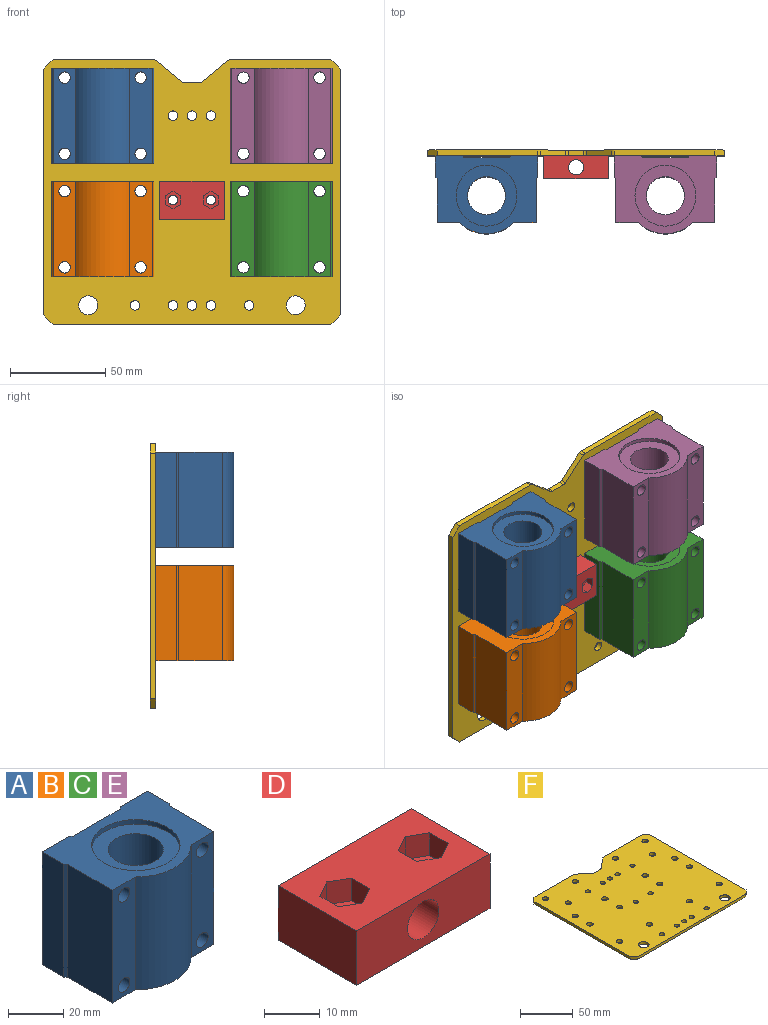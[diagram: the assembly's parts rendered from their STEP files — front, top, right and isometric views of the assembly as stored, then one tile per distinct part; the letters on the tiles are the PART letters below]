
ASSEMBLY  parts=6 mates=5
PART A: 25 faces, bbox 54x41x50 mm
  f0: cylinder r=10mm len=46mm, axis (0,0,1), area 2890.3mm2, adj f23,f24
  f1: cylinder r=16mm len=32mm, axis (0,0,1), area 201.1mm2, adj f22,f23
  f2: cylinder r=16mm len=32mm, axis (0,0,1), area 201.1mm2, adj f7,f24
  f3: cylinder r=3mm len=35mm, axis (0,-1,0), area 659.7mm2, adj f12,f16
  f4: cylinder r=3mm len=35mm, axis (0,-1,0), area 659.7mm2, adj f12,f16
  f5: cylinder r=3mm len=35mm, axis (0,-1,0), area 659.7mm2, adj f10,f20
  f6: cylinder r=3mm len=35mm, axis (0,-1,0), area 659.7mm2, adj f10,f20
  f7: plane 54x41mm, normal (0,0,-1), area 1132mm2, adj f2,f8,f9,f10,f11,f12,f13,f14
  f8: plane 50x1mm, normal (0.71,-0.71,0), area 70.7mm2, adj f7,f9,f21,f22
  f9: plane 50x23mm, normal (1,0,0), area 1150mm2, adj f7,f8,f10,f22
  f10: plane 50x11.72mm, normal (0,-1,0), area 529.3mm2, adj f5,f6,f7,f9,f11,f22
  f11: cylinder r=20mm len=50mm, axis (0,0,1), area 1590.8mm2, adj f7,f10,f12,f22
  f12: plane 50x11.72mm, normal (0,-1,0), area 529.3mm2, adj f3,f4,f7,f11,f13,f22
  f13: plane 50x23mm, normal (-1,0,0), area 1150mm2, adj f7,f12,f14,f22
  f14: plane 50x1mm, normal (-0.71,-0.71,0), area 70.7mm2, adj f7,f13,f15,f22
  f15: plane 50x11mm, normal (-1,0,0), area 550mm2, adj f7,f14,f16,f22
  f16: plane 50x14mm, normal (0,1,0), area 643.5mm2, adj f3,f4,f7,f15,f17,f22
  f17: plane 50x1mm, normal (0.71,0.71,0), area 70.7mm2, adj f7,f16,f18,f22
  f18: plane 50x24mm, normal (0,1,0), area 1200mm2, adj f7,f17,f19,f22
  f19: plane 50x1mm, normal (-0.71,0.71,0), area 70.7mm2, adj f7,f18,f20,f22
  f20: plane 50x14mm, normal (0,1,0), area 643.5mm2, adj f5,f6,f7,f19,f21,f22
  f21: plane 50x11mm, normal (1,0,0), area 550mm2, adj f7,f8,f20,f22
  f22: plane 54x41mm, normal (0,0,1), area 1132mm2, adj f1,f8,f9,f10,f11,f12,f13,f14
  f23: plane 32x32mm, normal (0,0,1), area 490.1mm2, adj f0,f1
  f24: plane 32x32mm, normal (0,0,-1), area 490.1mm2, adj f0,f2
PART B: same geometry as A
PART C: same geometry as A
PART D: 27 faces, bbox 34x20x12 mm
  f0: cylinder r=4.5mm len=9mm, axis (0,0,-1), area 56.5mm2, adj f6,f26
  f1: cylinder r=4.5mm len=9mm, axis (0,0,-1), area 56.5mm2, adj f6,f25
  f2: cylinder r=4mm len=20mm, axis (0,-1,0), area 502.7mm2, adj f9,f10
  f3: cylinder r=2.55mm len=5.1mm, axis (0,0,1), area 80.1mm2, adj f18,f25
  f4: cylinder r=2.55mm len=5.1mm, axis (0,0,1), area 80.1mm2, adj f11,f26
  f5: plane 20x12mm, normal (-1,0,0), area 240mm2, adj f6,f8,f9,f10
  f6: plane 34x20mm, normal (0,0,-1), area 552.8mm2, adj f0,f1,f5,f7,f9,f10
  f7: plane 20x12mm, normal (1,0,0), area 240mm2, adj f6,f8,f9,f10
  f8: plane 34x20mm, normal (0,0,1), area 569.1mm2, adj f5,f7,f9,f10,f12,f13,f14,f15
  f9: plane 34x12mm, normal (0,-1,0), area 357.7mm2, adj f2,f5,f6,f7,f8
  f10: plane 34x12mm, normal (0,1,0), area 357.7mm2, adj f2,f5,f6,f7,f8
  f11: plane 9.24x8mm, normal (0,0,1), area 35mm2, adj f4,f12,f13,f14,f15,f16,f17
  f12: plane 5x4mm, normal (-0.5,-0.87,0), area 23.1mm2, adj f8,f11,f13,f17
  f13: plane 5x4.62mm, normal (-1,0,0), area 23.1mm2, adj f8,f11,f12,f14
  f14: plane 5x4mm, normal (-0.5,0.87,0), area 23.1mm2, adj f8,f11,f13,f15
  f15: plane 5x4mm, normal (0.5,0.87,0), area 23.1mm2, adj f8,f11,f14,f16
  f16: plane 5x4.62mm, normal (1,0,0), area 23.1mm2, adj f8,f11,f15,f17
  f17: plane 5x4mm, normal (0.5,-0.87,0), area 23.1mm2, adj f8,f11,f12,f16
  f18: plane 9.24x8mm, normal (0,0,1), area 35mm2, adj f3,f19,f20,f21,f22,f23,f24
  f19: plane 5x4.62mm, normal (1,0,0), area 23.1mm2, adj f8,f18,f20,f24
  f20: plane 5x4mm, normal (0.5,-0.87,0), area 23.1mm2, adj f8,f18,f19,f21
  f21: plane 5x4mm, normal (-0.5,-0.87,0), area 23.1mm2, adj f8,f18,f20,f22
  f22: plane 5x4.62mm, normal (-1,0,0), area 23.1mm2, adj f8,f18,f21,f23
  f23: plane 5x4mm, normal (-0.5,0.87,0), area 23.1mm2, adj f8,f18,f22,f24
  f24: plane 5x4mm, normal (0.5,0.87,0), area 23.1mm2, adj f8,f18,f19,f23
  f25: plane 9x9mm, normal (0,0,-1), area 43.2mm2, adj f1,f3
  f26: plane 9x9mm, normal (0,0,-1), area 43.2mm2, adj f0,f4
PART E: same geometry as A
PART F: 50 faces, bbox 156x139.2x3 mm
  f0: plane 5x5mm, normal (-0.71,0.71,0), area 21.2mm2, adj f1,f46,f48,f49
  f1: plane 129.2x3mm, normal (-1,0,0), area 387.6mm2, adj f0,f2,f48,f49
  f2: plane 5x5mm, normal (-0.71,-0.71,0), area 21.2mm2, adj f1,f3,f48,f49
  f3: plane 146.01x3mm, normal (0,-1,0), area 438mm2, adj f2,f4,f48,f49
  f4: plane 5x5mm, normal (0.71,-0.71,0), area 21.2mm2, adj f3,f5,f48,f49
  f5: plane 129.2x3mm, normal (1,0,0), area 387.6mm2, adj f4,f6,f48,f49
  f6: plane 5x5mm, normal (0.71,0.71,0), area 21.2mm2, adj f5,f7,f48,f49
  f7: plane 52.66x3mm, normal (0,1,0), area 158mm2, adj f6,f8,f48,f49
  f8: cylinder r=2.35mm len=3mm, axis (0,0,-1), area 4.9mm2, adj f7,f9,f48,f49
  f9: plane 13.18x11.06mm, normal (-0.64,0.77,0), area 51.6mm2, adj f8,f10,f48,f49
  f10: cylinder r=2.35mm len=3mm, axis (0,0,-1), area 4.9mm2, adj f9,f11,f48,f49
  f11: plane 8.29x3mm, normal (0,1,0), area 24.9mm2, adj f10,f12,f48,f49
  f12: cylinder r=2.35mm len=3mm, axis (0,0,-1), area 4.9mm2, adj f11,f13,f48,f49
  f13: plane 13.18x11.06mm, normal (0.64,0.77,0), area 51.6mm2, adj f12,f14,f48,f49
  f14: cylinder r=2.35mm len=3mm, axis (0,0,-1), area 4.9mm2, adj f13,f46,f48,f49
  f15: cylinder r=2.5mm len=5mm, axis (0,0,-1), area 47.1mm2, adj f48,f49
  f16: cylinder r=2.5mm len=5mm, axis (0,0,-1), area 47.1mm2, adj f48,f49
  f17: cylinder r=2.5mm len=5mm, axis (0,0,-1), area 47.1mm2, adj f48,f49
  f18: cylinder r=2.5mm len=5mm, axis (0,0,-1), area 47.1mm2, adj f48,f49
  f19: cylinder r=2.5mm len=5mm, axis (0,0,-1), area 47.1mm2, adj f48,f49
  f20: cylinder r=5mm len=10mm, axis (0,0,-1), area 94.2mm2, adj f48,f49
  f21: cylinder r=5mm len=10mm, axis (0,0,-1), area 94.2mm2, adj f48,f49
  f22: cylinder r=3mm len=6mm, axis (0,0,-1), area 56.5mm2, adj f48,f49
  f23: cylinder r=3mm len=6mm, axis (0,0,-1), area 56.5mm2, adj f48,f49
  f24: cylinder r=3mm len=6mm, axis (0,0,-1), area 56.5mm2, adj f48,f49
  f25: cylinder r=3mm len=6mm, axis (0,0,-1), area 56.5mm2, adj f48,f49
  f26: cylinder r=3mm len=6mm, axis (0,0,-1), area 56.5mm2, adj f48,f49
  f27: cylinder r=3mm len=6mm, axis (0,0,-1), area 56.5mm2, adj f48,f49
  f28: cylinder r=3mm len=6mm, axis (0,0,-1), area 56.5mm2, adj f48,f49
  f29: cylinder r=3mm len=6mm, axis (0,0,-1), area 56.5mm2, adj f48,f49
  f30: cylinder r=3mm len=6mm, axis (0,0,-1), area 56.5mm2, adj f48,f49
  f31: cylinder r=3mm len=6mm, axis (0,0,-1), area 56.5mm2, adj f48,f49
  f32: cylinder r=3mm len=6mm, axis (0,0,-1), area 56.5mm2, adj f48,f49
  f33: cylinder r=3mm len=6mm, axis (0,0,-1), area 56.5mm2, adj f48,f49
  f34: cylinder r=3mm len=6mm, axis (0,0,-1), area 56.5mm2, adj f48,f49
  f35: cylinder r=3mm len=6mm, axis (0,0,-1), area 56.5mm2, adj f48,f49
  f36: cylinder r=3mm len=6mm, axis (0,0,-1), area 56.5mm2, adj f48,f49
  f37: cylinder r=3mm len=6mm, axis (0,0,-1), area 56.5mm2, adj f48,f49
  f38: cylinder r=3mm len=6mm, axis (0,0,-1), area 56.5mm2, adj f48,f49
  f39: cylinder r=3mm len=6mm, axis (0,0,-1), area 56.5mm2, adj f48,f49
  f40: cylinder r=2.5mm len=5mm, axis (0,0,-1), area 47.1mm2, adj f48,f49
  f41: cylinder r=2.5mm len=5mm, axis (0,0,-1), area 47.1mm2, adj f48,f49
  f42: cylinder r=2.5mm len=5mm, axis (0,0,-1), area 47.1mm2, adj f48,f49
  f43: cylinder r=2.5mm len=5mm, axis (0,0,-1), area 47.1mm2, adj f48,f49
  f44: cylinder r=2.5mm len=5mm, axis (0,0,-1), area 47.1mm2, adj f48,f49
  f45: cylinder r=2.5mm len=5mm, axis (0,0,-1), area 47.1mm2, adj f48,f49
  f46: plane 52.66x3mm, normal (0,1,0), area 158mm2, adj f0,f14,f48,f49
  f47: cylinder r=2.5mm len=5mm, axis (0,0,-1), area 47.1mm2, adj f48,f49
  f48: plane 156.01x139.2mm, normal (0,0,1), area 20467.3mm2, adj f0,f1,f2,f3,f4,f5,f6,f7
  f49: plane 156.01x139.2mm, normal (0,0,-1), area 20467.3mm2, adj f0,f1,f2,f3,f4,f5,f6,f7
PLACE A t=(-50.56,-145.89,16.67)mm
PLACE B t=(-50.56,-145.89,-43.03)mm
PLACE C t=(43.44,-145.89,-43.03)mm
PLACE D rot(axis=(1,0,0),90deg) t=(-4.27,-126.69,5.35)mm
PLACE E t=(43.44,-145.89,16.67)mm
PLACE F rot(axis=(1,0,0),90deg) t=(690.73,-117.69,-577.63)mm
MATE fastened D.f1 <-> F.f40  axis (0,1,0) through (5.73,-120.69,-4.65)mm
MATE fastened B.f4 <-> F.f23  axis (0,-1,0) through (-71.27,-120.69,-0.03)mm
MATE fastened E.f5 <-> F.f26  axis (0,1,0) through (62.73,-120.69,59.67)mm
MATE fastened A.f4 <-> F.f24  axis (0,-1,0) through (-71.27,-120.69,59.67)mm
MATE fastened C.f5 <-> F.f29  axis (0,1,0) through (62.73,-120.69,-0.03)mm
